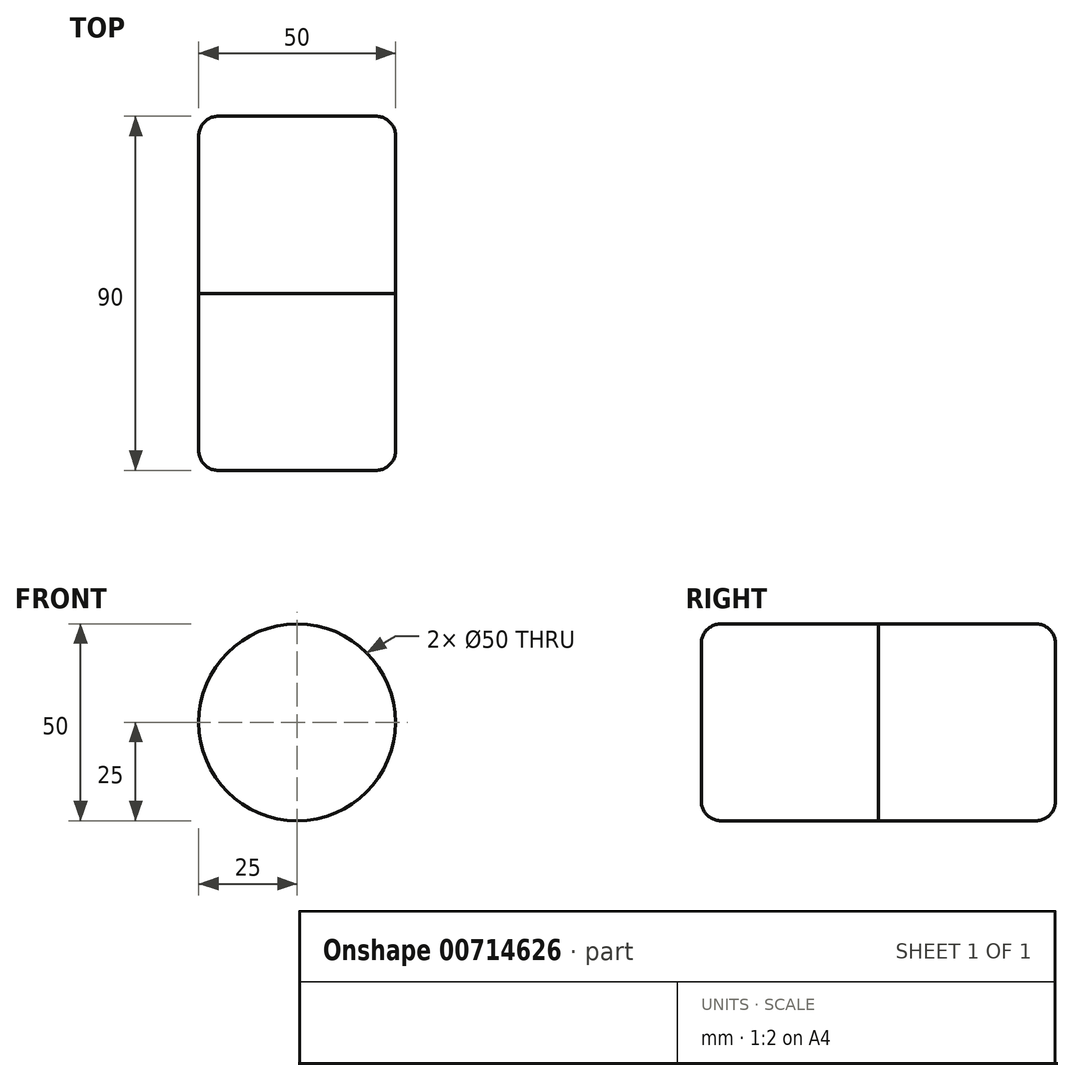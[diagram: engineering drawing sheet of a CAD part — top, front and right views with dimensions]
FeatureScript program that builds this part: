
annotation { "Feature Type Name" : "Feature", "Feature Type Description" : "" }
export const myFeature = defineFeature(function(context is Context, id is Id, definition is map)
    precondition{}
    {
        {
            var Q0;
            Q0=qCreatedBy(makeId("Top.planeOp"),FACE);
            var sketch = newSketch(context, id + "F0", { "sketchPlane" : qUnion([Q0])});
            skLineSegment(sketch, "E0", {"start": v(25, 0) * mm, "end": v(25, 45) * mm});
            skLineSegment(sketch, "E1", {"start": v(25, 45) * mm, "end": v(0, 45) * mm});
            skLineSegment(sketch, "E2", {"start": v(0, 0) * mm, "end": v(0, 125.05) * mm, "construction": true});
            skLineSegment(sketch, "E3", {"start": v(0, 0) * mm, "end": v(71.52, 0) * mm, "construction": true});
            skSolve(sketch);
        }
        {
            var Q0;
            Q0=sQuery(id+"F0.wireOp",EDGE,"E1");
            var Q1;
            Q1=sQuery(id+"F0.wireOp",EDGE,"E0");
            var Q2;
            Q2=sQuery(id+"F0.wireOp",EDGE,"E2");
            revolve(context, id + "F1", {"bodyType" : ToolBodyType.SURFACE, "surfaceOperationType" : NewSurfaceOperationType.NEW, "surfaceEntities" : qUnion([Q0, Q1]), "axis" : qUnion([Q2]), "revolveType" : RevolveType.FULL});
        }
        {
            var Q0;
            Q0=makeQuery(id+"F1.opRevolve","SWEPT_EDGE",EDGE,{"disambiguationData":[OSD([sQuery(id+"F0.wireOp",VERTEX,"E0.end")])]});
            fillet(context, id + "F2", {"entities" : qUnion([Q0]), "radius" : 5 * mm, "tangentPropagation" : true, "allowEdgeOverflow" : false});
        }
        {
            var Q0;
            Q0=makeQuery(id+"F1.opRevolve","SWEPT_BODY",BODY,{"disambiguationData":[OSD([sQuery(id+"F0.wireOp",EDGE,"E0")])]});
            var Q1;
            Q1=qCreatedBy(makeId("Front.planeOp"),FACE);
            mirror(context, id + "F3", {"entities" : qUnion([Q0]), "mirrorPlane" : qUnion([Q1])});
        }
    });
